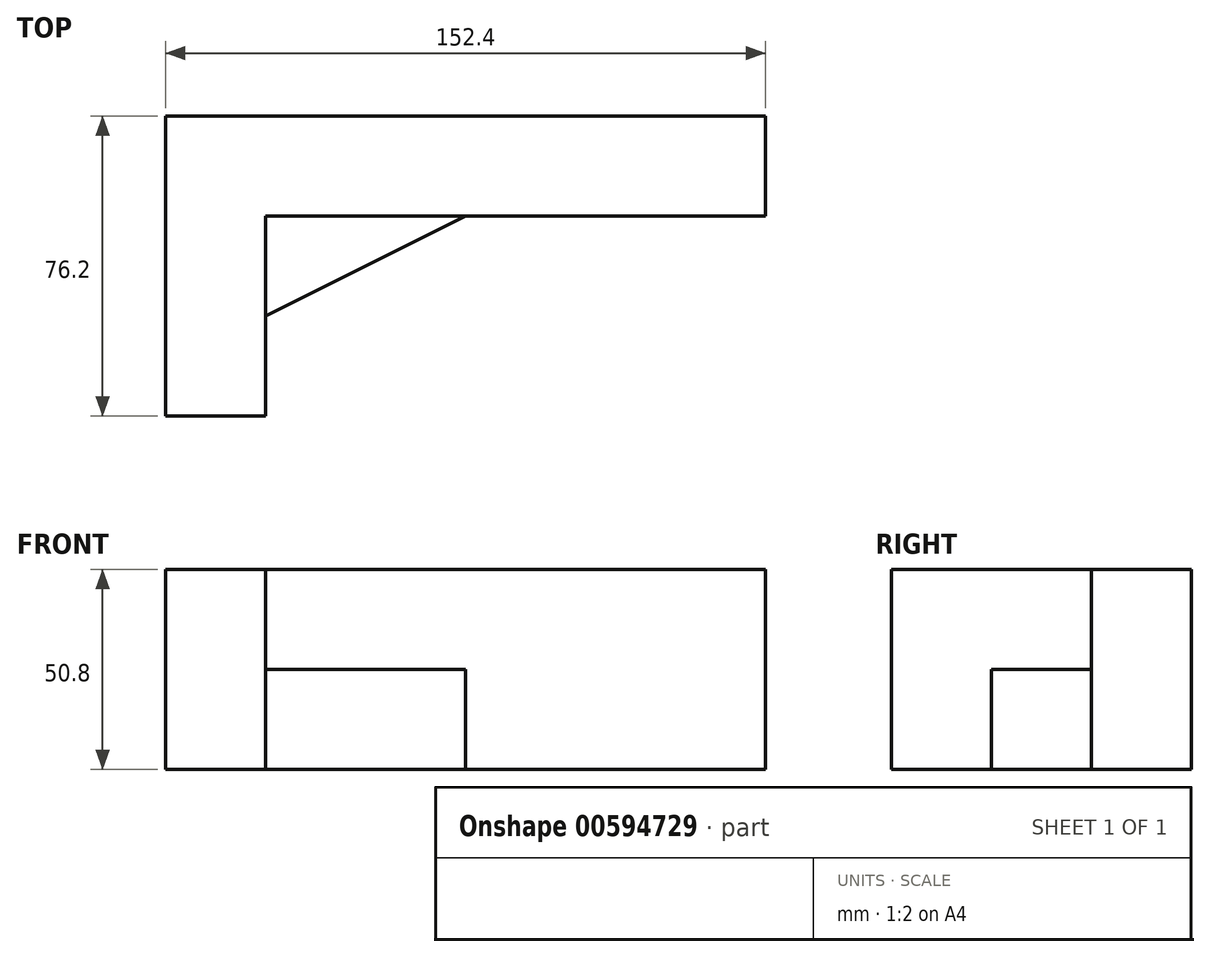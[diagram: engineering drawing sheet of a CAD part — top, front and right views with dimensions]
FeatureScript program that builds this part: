
annotation { "Feature Type Name" : "Feature", "Feature Type Description" : "" }
export const myFeature = defineFeature(function(context is Context, id is Id, definition is map)
    precondition{}
    {
        {
            var Q0;
            Q0=qCreatedBy(makeId("Top.planeOp"),FACE);
            var sketch = newSketch(context, id + "F0", { "sketchPlane" : qUnion([Q0])});
            skLineSegment(sketch, "E0.bottom", {"start": v(0, 0) * mm, "end": v(25.4, 0) * mm});
            skLineSegment(sketch, "E0.top", {"start": v(0, 76.2) * mm, "end": v(152.4, 76.2) * mm});
            skLineSegment(sketch, "E0.left", {"start": v(0, 0) * mm, "end": v(0, 76.2) * mm});
            skLineSegment(sketch, "E0.right", {"start": v(152.4, 50.8) * mm, "end": v(152.4, 76.2) * mm});
            skLineSegment(sketch, "E1", {"start": v(25.4, 0) * mm, "end": v(25.4, 50.8) * mm});
            skLineSegment(sketch, "E2", {"start": v(25.4, 50.8) * mm, "end": v(152.4, 50.8) * mm});
            skLineSegment(sketch, "E3", {"start": v(152.4, 50.8) * mm, "end": v(76.2, 50.8) * mm});
            skLineSegment(sketch, "E4", {"start": v(25.4, 25.4) * mm, "end": v(76.2, 50.8) * mm});
            skLineSegment(sketch, "E5", {"start": v(25.4, 25.4) * mm, "end": v(25.4, 50.8) * mm});
            skLineSegment(sketch, "E6", {"start": v(76.2, 50.8) * mm, "end": v(25.4, 50.8) * mm});
            skSolve(sketch);
        }
        {
            var Q0;
            {var subQ2=sQuery(id+"F0.wireOp",EDGE,"E0.top");Q0=makeQuery(id+"F0.imprint","IMPRINT",FACE,{"disambiguationData":[TD([[makeQuery(id+"F0.imprint","IMPRINT",EDGE,{"derivedFrom":subQ2}),-1.0]])]});}
            extrude(context, id + "F1", {"entities" : qUnion([Q0]), "depth" : 50.8 * mm, "offsetDistance" : 25.4 * mm});
        }
        {
            var Q0;
            Q0=makeQuery(id+"F0.imprint","IMPRINT",FACE,{"disambiguationData":[TD([[makeQuery(id+"F0.imprint","IMPRINT",EDGE,{"derivedFrom":sQuery(id+"F0.wireOp",EDGE,"E4")}),1.0]])]});
            extrude(context, id + "F2", {"entities" : qUnion([Q0]), "operationType" : NewBodyOperationType.ADD, "depth" : 25.4 * mm, "offsetDistance" : 25.4 * mm});
        }
    });
